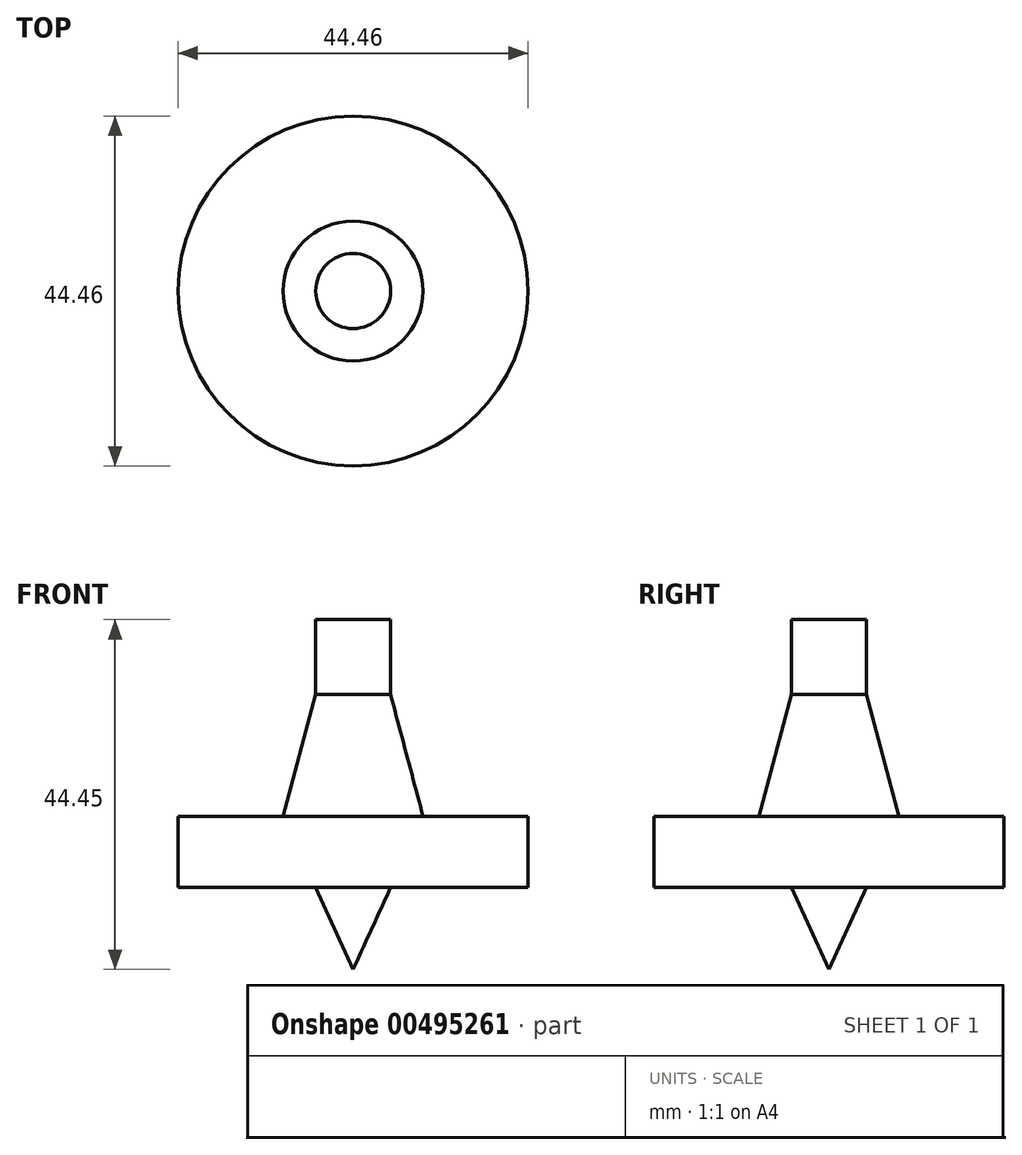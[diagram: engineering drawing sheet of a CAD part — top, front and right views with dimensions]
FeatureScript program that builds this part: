
annotation { "Feature Type Name" : "Feature", "Feature Type Description" : "" }
export const myFeature = defineFeature(function(context is Context, id is Id, definition is map)
    precondition{}
    {
        {
            var Q0;
            Q0=qCreatedBy(makeId("Front.planeOp"),FACE);
            var sketch = newSketch(context, id + "F0", { "sketchPlane" : qUnion([Q0])});
            skLineSegment(sketch, "E0", {"start": v(0, 34.05) * mm, "end": v(4.76, 34.05) * mm});
            skLineSegment(sketch, "E1", {"start": v(4.76, 34.05) * mm, "end": v(4.76, 24.53) * mm});
            skLineSegment(sketch, "E2", {"start": v(4.76, 0) * mm, "end": v(0, -10.4) * mm});
            skLineSegment(sketch, "E3.MirrorCS", {"start": v(-4.76, 0) * mm, "end": v(0, -10.4) * mm});
            skLineSegment(sketch, "E4.MirrorCS", {"start": v(-4.76, 34.05) * mm, "end": v(-4.76, 24.53) * mm});
            skLineSegment(sketch, "E5.MirrorCS", {"start": v(0, 34.05) * mm, "end": v(-4.76, 34.05) * mm});
            skLineSegment(sketch, "E6", {"start": v(4.76, 0) * mm, "end": v(22.23, 0) * mm});
            skLineSegment(sketch, "E7", {"start": v(22.23, 0) * mm, "end": v(22.23, 9.01) * mm});
            skLineSegment(sketch, "E8", {"start": v(22.23, 9.01) * mm, "end": v(8.89, 9.01) * mm});
            skLineSegment(sketch, "E9.MirrorCS", {"start": v(-22.23, 9.01) * mm, "end": v(-8.89, 9.01) * mm});
            skLineSegment(sketch, "E10.MirrorCS", {"start": v(-22.23, 0) * mm, "end": v(-22.23, 9.01) * mm});
            skLineSegment(sketch, "E11.MirrorCS", {"start": v(-4.76, 0) * mm, "end": v(-22.23, 0) * mm});
            skLineSegment(sketch, "E12", {"start": v(4.76, 24.53) * mm, "end": v(8.89, 9.01) * mm});
            skLineSegment(sketch, "E13", {"start": v(-4.76, 24.53) * mm, "end": v(-8.89, 9.01) * mm});
            skLineSegment(sketch, "E14", {"start": v(0, 34.05) * mm, "end": v(0, -10.4) * mm});
            skSolve(sketch);
        }
        {
            var Q0;
            Q0=makeQuery(id+"F0.imprint","IMPRINT",FACE,{"disambiguationData":[TD([[makeQuery(id+"F0.imprint","IMPRINT",EDGE,{"derivedFrom":sQuery(id+"F0.wireOp",EDGE,"E0")}),-1.0]])]});
            var Q1;
            Q1=sQuery(id+"F0.wireOp",EDGE,"E14");
            revolve(context, id + "F1", {"entities" : qUnion([Q0]), "axis" : qUnion([Q1]), "revolveType" : RevolveType.FULL});
        }
    });
